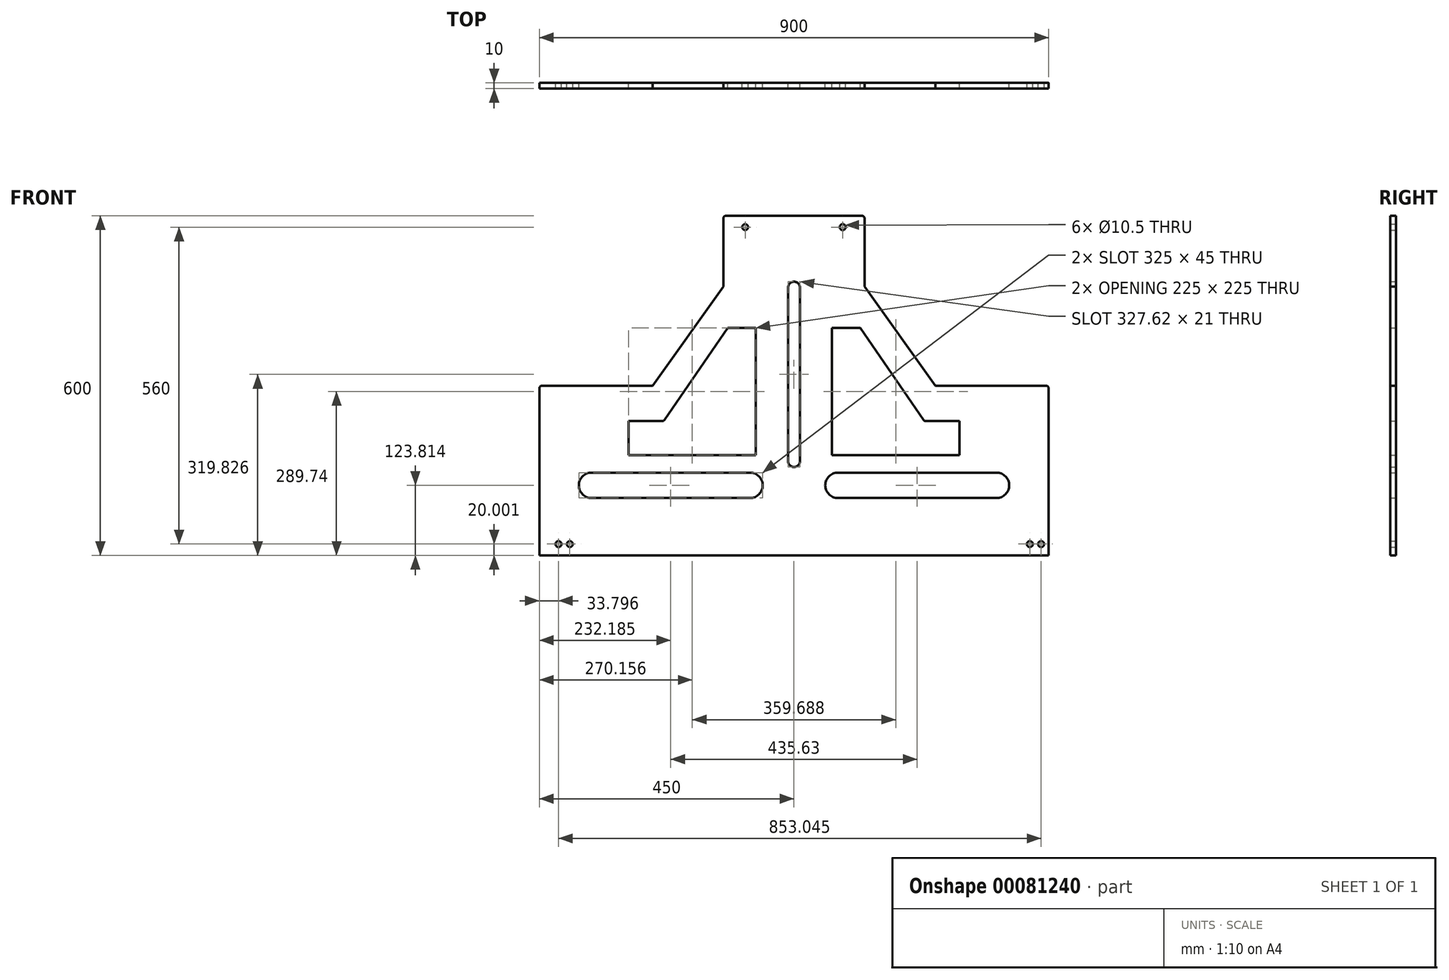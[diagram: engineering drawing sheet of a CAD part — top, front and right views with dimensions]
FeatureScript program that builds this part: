
annotation { "Feature Type Name" : "Feature", "Feature Type Description" : "" }
export const myFeature = defineFeature(function(context is Context, id is Id, definition is map)
    precondition{}
    {
        {
            var Q0;
            Q0=qCreatedBy(makeId("Front.planeOp"),FACE);
            var sketch = newSketch(context, id + "F0", { "sketchPlane" : qUnion([Q0])});
            skLineSegment(sketch, "E0", {"start": v(-450, 62.76) * mm, "end": v(-450, -237.24) * mm});
            skLineSegment(sketch, "E1", {"start": v(-450, -237.24) * mm, "end": v(0, -237.24) * mm});
            skLineSegment(sketch, "E2", {"start": v(-450, 62.76) * mm, "end": v(-250, 62.76) * mm});
            skLineSegment(sketch, "E3", {"start": v(-250, 62.76) * mm, "end": v(-125, 237.76) * mm});
            skLineSegment(sketch, "E4.MirrorCS", {"start": v(450, 62.76) * mm, "end": v(250, 62.76) * mm});
            skLineSegment(sketch, "E5.MirrorCS", {"start": v(450, 62.76) * mm, "end": v(450, -237.24) * mm});
            skLineSegment(sketch, "E6.MirrorCS", {"start": v(450, -237.24) * mm, "end": v(0, -237.24) * mm});
            skLineSegment(sketch, "E7.MirrorCS", {"start": v(250, 62.76) * mm, "end": v(125, 237.76) * mm});
            skLineSegment(sketch, "E8", {"start": v(125, 237.76) * mm, "end": v(125, 362.76) * mm});
            skLineSegment(sketch, "E9.MirrorCS", {"start": v(-125, 237.76) * mm, "end": v(-125, 362.76) * mm});
            skLineSegment(sketch, "E10", {"start": v(-125, 362.76) * mm, "end": v(125, 362.76) * mm});
            skPoint(sketch, "E11.orphan", {"position": v(0, 412.76) * mm});
            skCircle(sketch, "E12", {"center": v(86.05, 342.76) * mm, "radius": 5.25 * mm});
            skCircle(sketch, "E13", {"center": v(-86.26, 342.76) * mm, "radius": 5.25 * mm});
            skLineSegment(sketch, "E14", {"start": v(-77.82, -90.93) * mm, "end": v(-357.82, -90.93) * mm});
            skLineSegment(sketch, "E15", {"start": v(-77.82, -135.93) * mm, "end": v(-357.82, -135.93) * mm});
            skLineSegment(sketch, "E16.MirrorCS", {"start": v(77.82, -90.93) * mm, "end": v(357.82, -90.93) * mm});
            skLineSegment(sketch, "E17.MirrorCS", {"start": v(77.82, -135.93) * mm, "end": v(357.82, -135.93) * mm});
            skArc(sketch, "E18", {"start": v(357.82, -90.93) * mm, "mid": v(380.32, -113.43) * mm, "end": v(357.82, -135.93) * mm});
            skArc(sketch, "E19", {"start": v(77.82, -90.93) * mm, "mid": v(55.32, -113.43) * mm, "end": v(77.82, -135.93) * mm});
            skArc(sketch, "E20", {"start": v(-77.82, -90.93) * mm, "mid": v(-55.32, -113.43) * mm, "end": v(-77.82, -135.93) * mm});
            skLineSegment(sketch, "E21", {"start": v(-10.5, 235.9) * mm, "end": v(-10.5, 0) * mm});
            skArc(sketch, "E22", {"start": v(-357.82, -90.93) * mm, "mid": v(-380.32, -113.43) * mm, "end": v(-357.82, -135.93) * mm});
            skLineSegment(sketch, "E23.bottom", {"start": v(-292.34, 0) * mm, "end": v(-230.37, 0) * mm});
            skLineSegment(sketch, "E23.top", {"start": v(-292.34, -60) * mm, "end": v(-67.34, -60) * mm});
            skLineSegment(sketch, "E23.left", {"start": v(-292.34, 0) * mm, "end": v(-292.34, -60) * mm});
            skLineSegment(sketch, "E23.right", {"start": v(-67.34, 0) * mm, "end": v(-67.34, -60) * mm});
            skLineSegment(sketch, "E24", {"start": v(-67.34, 0) * mm, "end": v(-67.34, 165) * mm});
            skLineSegment(sketch, "E25", {"start": v(-67.34, 165) * mm, "end": v(-117.34, 165) * mm});
            skLineSegment(sketch, "E26", {"start": v(-117.34, 165) * mm, "end": v(-230.37, 0) * mm});
            skLineSegment(sketch, "E27.MirrorCS", {"start": v(67.34, 165) * mm, "end": v(117.34, 165) * mm});
            skLineSegment(sketch, "E28.MirrorCS", {"start": v(117.34, 165) * mm, "end": v(230.37, 0) * mm});
            skLineSegment(sketch, "E29.MirrorCS", {"start": v(292.34, 0) * mm, "end": v(230.37, 0) * mm});
            skLineSegment(sketch, "E30.MirrorCS", {"start": v(292.34, -60) * mm, "end": v(67.34, -60) * mm});
            skLineSegment(sketch, "E31.MirrorCS", {"start": v(67.34, 0) * mm, "end": v(67.34, 165) * mm});
            skLineSegment(sketch, "E32.MirrorCS", {"start": v(67.34, 0) * mm, "end": v(67.34, -60) * mm});
            skLineSegment(sketch, "E33.MirrorCS", {"start": v(292.34, 0) * mm, "end": v(292.34, -60) * mm});
            skCircle(sketch, "E34", {"center": v(-416.2, -217.24) * mm, "radius": 5.25 * mm});
            skCircle(sketch, "E35", {"center": v(416.84, -217.24) * mm, "radius": 5.25 * mm});
            skPoint(sketch, "E36.orphan", {"position": v(0, -202.88) * mm});
            skLineSegment(sketch, "E37.MirrorCS", {"start": v(10.5, 235.9) * mm, "end": v(10.5, 0) * mm});
            skPoint(sketch, "E38.MirrorCS.end.orphan", {"position": v(-21, 63.33) * mm});
            skPoint(sketch, "E38.MirrorCS.start.orphan", {"position": v(-21, 362.76) * mm});
            skPoint(sketch, "E39.orphan", {"position": v(0, 362.76) * mm});
            skPoint(sketch, "E40.start.orphan", {"position": v(0, 235.9) * mm});
            skPoint(sketch, "E41.start.orphan", {"position": v(0, 63.33) * mm});
            skArc(sketch, "E42", {"start": v(-10.5, 235.9) * mm, "mid": v(0, 246.4) * mm, "end": v(10.5, 235.9) * mm});
            skLineSegment(sketch, "E43", {"start": v(10.5, 0) * mm, "end": v(10.5, -70.73) * mm});
            skLineSegment(sketch, "E44", {"start": v(-10.5, 0) * mm, "end": v(-10.5, -70.73) * mm});
            skPoint(sketch, "E44.endSnap0", {"position": v(-6.21, -70.73) * mm});
            skPoint(sketch, "E45.orphan", {"position": v(-22.92, -70.73) * mm});
            skArc(sketch, "E46", {"start": v(10.5, -70.73) * mm, "mid": v(0, -81.23) * mm, "end": v(-10.5, -70.73) * mm});
            skCircle(sketch, "E47", {"center": v(-396.2, -217.24) * mm, "radius": 5.25 * mm});
            skCircle(sketch, "E48", {"center": v(436.84, -217.24) * mm, "radius": 5.25 * mm});
            skSolve(sketch);
        }
        {
            var Q0;
            Q0=makeQuery(id+"F0.imprint","IMPRINT",FACE,{"disambiguationData":[TD([[makeQuery(id+"F0.imprint","IMPRINT",EDGE,{"derivedFrom":sQuery(id+"F0.wireOp",EDGE,"E0")}),1.0]])]});
            extrude(context, id + "F1", {"entities" : qUnion([Q0]), "depth" : 10 * mm});
        }
        {
            var Q0;
            Q0=makeQuery(id+"F1.opExtrude","SWEPT_EDGE",EDGE,{"disambiguationData":[OSD([sQuery(id+"F0.wireOp",EDGE,"E23.bottom"),sQuery(id+"F0.wireOp",EDGE,"E26")])]});
            var Q1;
            Q1=makeQuery(id+"F1.opExtrude","SWEPT_EDGE",EDGE,{"disambiguationData":[OSD([sQuery(id+"F0.wireOp",EDGE,"E28.MirrorCS"),sQuery(id+"F0.wireOp",EDGE,"E29.MirrorCS")])]});
            fillet(context, id + "F2", {"entities" : qUnion([Q0, Q1]), "radius" : 5 * mm, "tangentPropagation" : true, "allowEdgeOverflow" : false});
        }
        {
            var Q0;
            Q0=makeQuery(id+"F1.opExtrude","SWEPT_EDGE",EDGE,{"disambiguationData":[OSD([sQuery(id+"F0.wireOp",EDGE,"E0"),sQuery(id+"F0.wireOp",EDGE,"E2")])]});
            var Q1;
            Q1=makeQuery(id+"F1.opExtrude","SWEPT_EDGE",EDGE,{"disambiguationData":[OSD([sQuery(id+"F0.wireOp",EDGE,"E9.MirrorCS"),sQuery(id+"F0.wireOp",EDGE,"E10")])]});
            var Q2;
            Q2=makeQuery(id+"F1.opExtrude","SWEPT_EDGE",EDGE,{"disambiguationData":[OSD([sQuery(id+"F0.wireOp",EDGE,"E8"),sQuery(id+"F0.wireOp",EDGE,"E10")])]});
            var Q3;
            Q3=makeQuery(id+"F1.opExtrude","SWEPT_EDGE",EDGE,{"disambiguationData":[OSD([sQuery(id+"F0.wireOp",EDGE,"E4.MirrorCS"),sQuery(id+"F0.wireOp",EDGE,"E5.MirrorCS")])]});
            fillet(context, id + "F3", {"entities" : qUnion([Q0, Q1, Q2, Q3]), "radius" : 5 * mm, "tangentPropagation" : true, "allowEdgeOverflow" : false});
        }
    });
